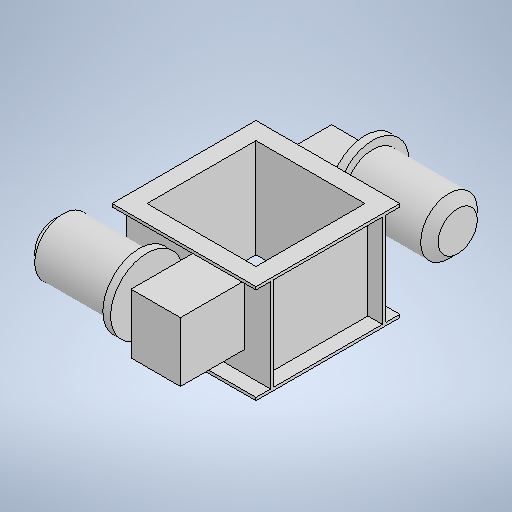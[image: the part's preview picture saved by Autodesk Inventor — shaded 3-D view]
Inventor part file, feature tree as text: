
AUTODESK INVENTOR PART (.ipt)
format: ipt  version: 2025 (Build 290162010, 162A)  size: 347,136 bytes
history: native  units: mm
features: extrude x8, sketch x8, chamfer x2, pattern_circular x1
ambient origin geometry x8: Origin, YZ Plane, XZ Plane, XY Plane, X Axis, Y Axis, Z Axis, Center Point
bodies: Solid1 (feature_tree)
feature tree (19):
  extrude  "Extrusion1"  Depth=495.0mm
  extrude  "Extrusion2"  Depth=395.0mm
  extrude  "Extrusion3"  Depth=320.0mm TaperAngle=0.0deg
  extrude  "Extrusion4"  Depth=495.0mm
  extrude  "Extrusion5"  Depth=375.0mm
  extrude  "Extrusion6"  TaperAngle=0.0deg  [1 undecoded]
  extrude  "Extrusion7"  Depth=10.0mm
  pattern_circular  "Circular Pattern1"  [2 undecoded]
  extrude  "Extrusion8"  Depth=205.0mm
  chamfer  "Chamfer1"  Distance=170.0mm
  chamfer  "Chamfer2"  Distance=175.0mm
  sketch  "Sketch1"  dims[d0=495.0mm d1=495.0mm]
  sketch  "Sketch2"  dims[d2=10.0mm d3=0.0mm d4=395.0mm]
  sketch  "Sketch3"  dims[d5=395.0mm d6=320.0mm d7=0.0mm]
  sketch  "Sketch4"  dims[d8=495.0mm d9=495.0mm]
  sketch  "Sketch6"  dims[d10=10.0mm d11=0.0mm d12=375.0mm]
  sketch  "Sketch7"  dims[d13=375.0mm d14=0.0mm d15=0.0mm]
  sketch  "Sketch8"  dims[d19=10.0mm d20=10.0mm]
  sketch  "Sketch10"  dims[d21=10.0mm d22=10.0mm d23=205.0mm d24=170.0mm d25=175.0mm d26=185.0mm d27=220.0mm d28=0.0mm d30=250.0mm d33=45.0mm d34=55.0mm d35=27.0mm d36=0.0mm d37=195.0mm d39=292.0mm d40=0.0mm d41=20.0mm d42=360.0deg d44=165.0mm d45=87.0mm d46=55.0mm d47=125.0mm d48=0.0mm d49=30.0mm d50=2.0mm d51=45.0deg d52=30.0mm d53=2.0mm d54=45.0deg]
note: 3 required parameter values undecoded (feature->parameter linkage not recoverable at this tier; creation-order binding heuristic only, values carry confidence <= 0.55)
